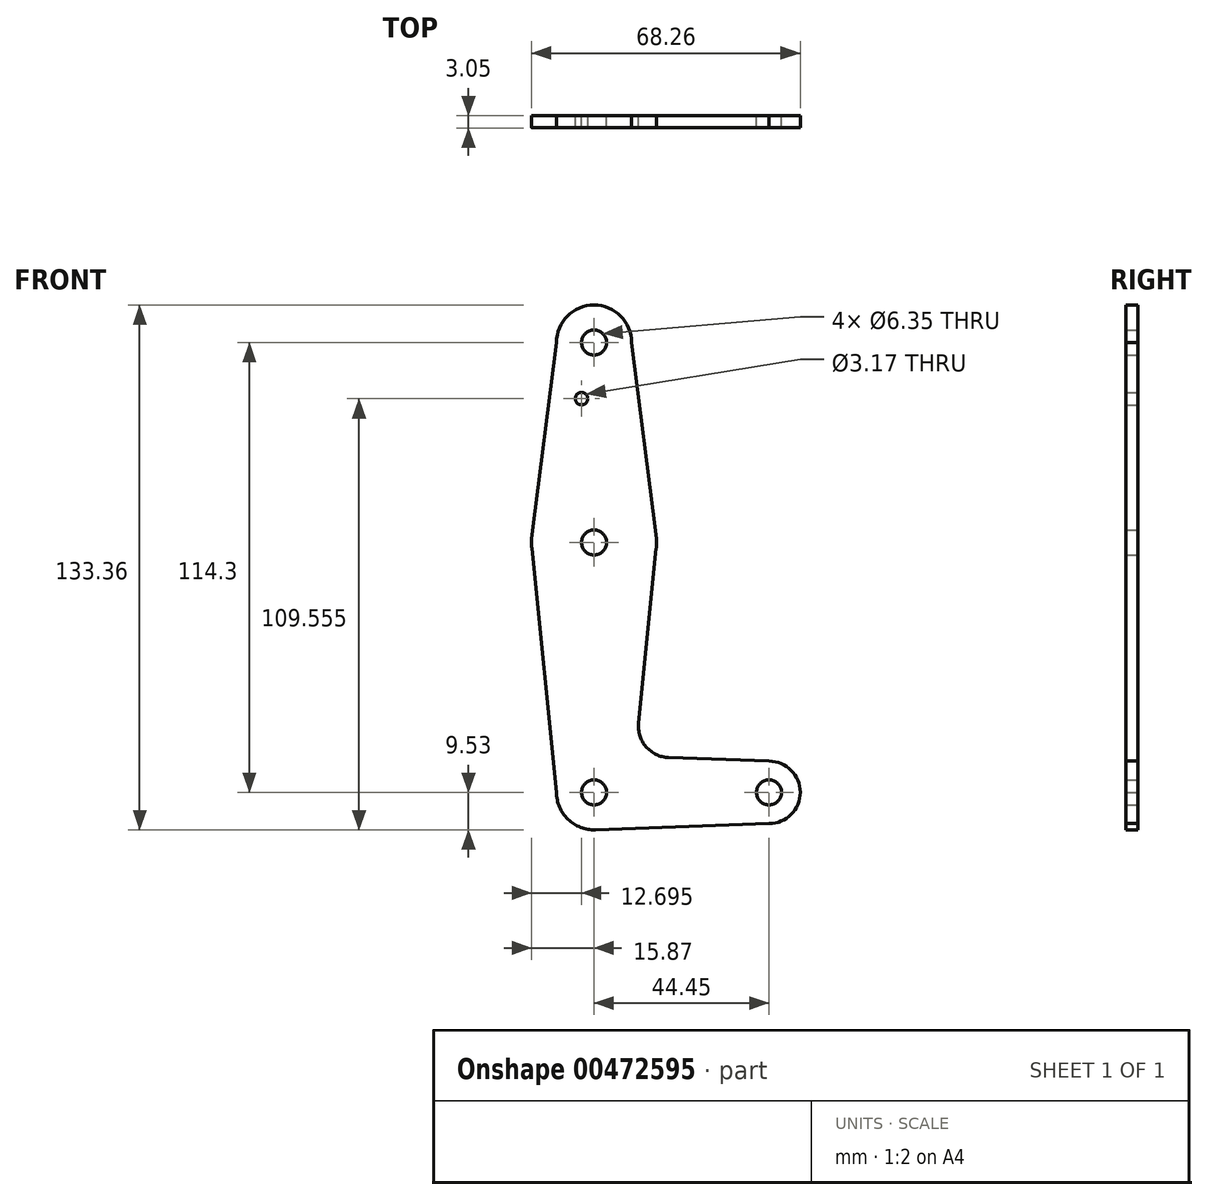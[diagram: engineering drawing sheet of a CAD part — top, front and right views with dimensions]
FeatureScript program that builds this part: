
annotation { "Feature Type Name" : "Feature", "Feature Type Description" : "" }
export const myFeature = defineFeature(function(context is Context, id is Id, definition is map)
    precondition{}
    {
        {
            var Q0;
            Q0=qCreatedBy(makeId("Front.planeOp"),FACE);
            var sketch = newSketch(context, id + "F0", { "sketchPlane" : qUnion([Q0])});
            skLineSegment(sketch, "E0", {"start": v(0, 0) * mm, "end": v(0, 63.5) * mm, "construction": true});
            skCircle(sketch, "E1", {"center": v(0, 63.5) * mm, "radius": 15.88 * mm});
            skCircle(sketch, "E2", {"center": v(0, 0) * mm, "radius": 9.53 * mm});
            skLineSegment(sketch, "E3", {"start": v(0, 63.5) * mm, "end": v(0, 114.3) * mm, "construction": true});
            skCircle(sketch, "E4", {"center": v(0, 114.3) * mm, "radius": 9.53 * mm});
            skLineSegment(sketch, "E5", {"start": v(0, 0) * mm, "end": v(44.45, 0) * mm, "construction": true});
            skCircle(sketch, "E6", {"center": v(44.45, 0) * mm, "radius": 7.94 * mm});
            skLineSegment(sketch, "E7", {"start": v(-9.53, 114.3) * mm, "end": v(-15.75, 65.5) * mm});
            skLineSegment(sketch, "E8", {"start": v(9.53, 114.3) * mm, "end": v(15.75, 65.5) * mm});
            skLineSegment(sketch, "E9", {"start": v(-9.52, 0) * mm, "end": v(-15.8, 61.9) * mm});
            skCircle(sketch, "E10", {"center": v(0, 114.3) * mm, "radius": 3.17 * mm});
            skCircle(sketch, "E11", {"center": v(0, 63.5) * mm, "radius": 3.17 * mm});
            skCircle(sketch, "E12", {"center": v(44.45, 0) * mm, "radius": 3.17 * mm});
            skCircle(sketch, "E13", {"center": v(-3.17, 100.03) * mm, "radius": 1.59 * mm});
            skCircle(sketch, "E14", {"center": v(0, 0) * mm, "radius": 3.18 * mm});
            skLineSegment(sketch, "E15", {"start": v(11.3, 17.6) * mm, "end": v(15.8, 61.9) * mm});
            skLineSegment(sketch, "E16", {"start": v(44.45, -7.94) * mm, "end": v(0, -9.53) * mm});
            skLineSegment(sketch, "E17", {"start": v(44.45, 7.94) * mm, "end": v(18.93, 8.85) * mm});
            skPoint(sketch, "E18.newPointA", {"position": v(9.52, 0) * mm});
            skPoint(sketch, "E18.newPointB", {"position": v(0, 9.53) * mm});
            skArc(sketch, "E18.filletArc", {"start": v(11.3, 17.6) * mm, "mid": v(13.22, 11.57) * mm, "end": v(18.93, 8.85) * mm});
            skSolve(sketch);
        }
        {
            var Q0;
            Q0 = qSketchRegion(id + "F0", true);
            extrude(context, id + "F1", {"entities" : qUnion([Q0]), "depth" : 3.05 * mm});
        }
    });
